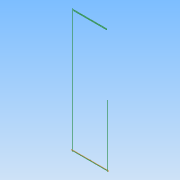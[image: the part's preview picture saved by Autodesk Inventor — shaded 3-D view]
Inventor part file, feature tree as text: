
AUTODESK INVENTOR PART (.ipt)
format: ipt  version: 2013 (Build 170138000, 138)  size: 326,656 bytes
history: native  units: in
note: dims shown in document units (in); Inventor stores cm internally (conversion verified against a paired STEP export)
features: reference x7, extrude x2, sketch x2, plane x1
ambient origin geometry x8: Origin, YZ Plane, XZ Plane, XY Plane, X Axis, Y Axis, Z Axis, Center Point
bodies: Solid1 (feature_tree)
feature tree (12):
  plane  "Work Plane1"
  extrude  "Extrusion1"  Depth=0.0938in
  extrude  "Extrusion2"  Depth=1.0in TaperAngle=0.0deg
  sketch  "Sketch1"  dims[d0=0.0938in d1=0.0938in]
  reference  "Reference1"
  reference  "Reference2"
  reference  "Reference3"
  reference  "Reference4"
  reference  "Reference5"
  reference  "Reference6"
  reference  "Reference7"
  sketch  "Sketch2"  dims[d2=0.22in d3=0.0in d4=1.0in d5=0.0in]
